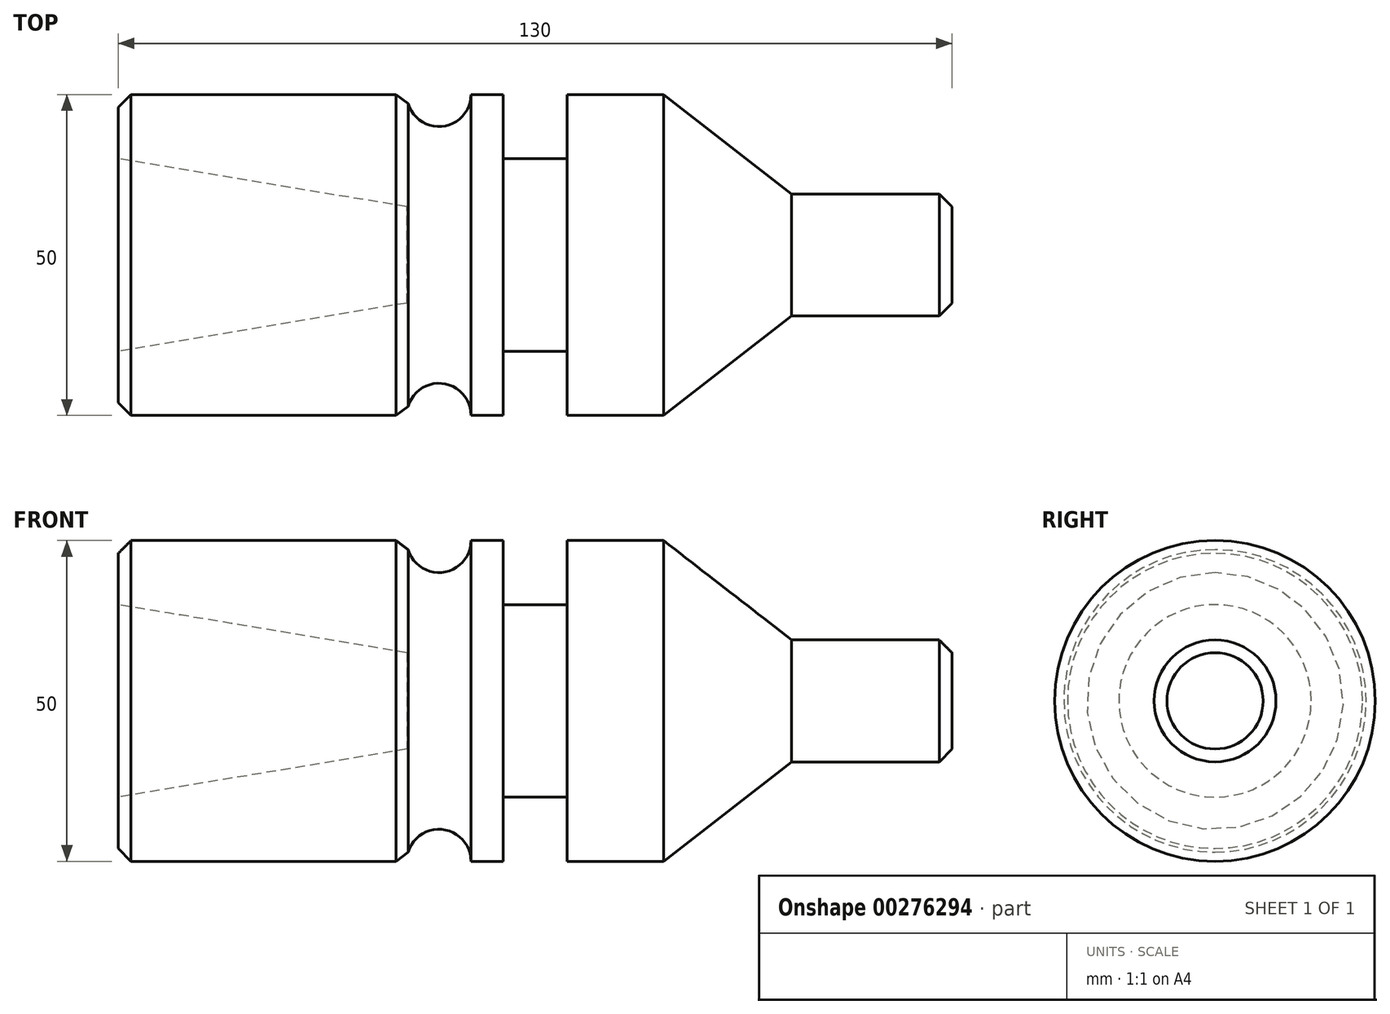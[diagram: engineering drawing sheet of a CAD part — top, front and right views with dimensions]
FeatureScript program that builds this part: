
annotation { "Feature Type Name" : "Feature", "Feature Type Description" : "" }
export const myFeature = defineFeature(function(context is Context, id is Id, definition is map)
    precondition{}
    {
        {
            var Q0;
            Q0=qCreatedBy(makeId("Front.planeOp"),FACE);
            var sketch = newSketch(context, id + "F0", { "sketchPlane" : qUnion([Q0])});
            skLineSegment(sketch, "E0.top", {"start": v(-62.42, 25) * mm, "end": v(-17.42, 25) * mm});
            skLineSegment(sketch, "E0.left", {"start": v(-62.42, 15) * mm, "end": v(-62.42, 25) * mm});
            skLineSegment(sketch, "E0.right", {"start": v(67.58, 0) * mm, "end": v(67.58, 9.5) * mm});
            skLineSegment(sketch, "E1", {"start": v(-62.42, 25) * mm, "end": v(-62.42, 15) * mm});
            skLineSegment(sketch, "E2", {"start": v(-17.42, 7.5) * mm, "end": v(-17.42, 0) * mm, "construction": true});
            skLineSegment(sketch, "E3", {"start": v(-17.42, 0) * mm, "end": v(-17.42, 7.5) * mm});
            skLineSegment(sketch, "E4", {"start": v(-62.42, 15) * mm, "end": v(-17.42, 7.5) * mm});
            skArc(sketch, "E5", {"start": v(-17.42, 25) * mm, "mid": v(-12.42, 20) * mm, "end": v(-7.42, 25) * mm});
            skLineSegment(sketch, "E6", {"start": v(-7.42, 25) * mm, "end": v(-2.42, 25) * mm});
            skLineSegment(sketch, "E7", {"start": v(-2.42, 25) * mm, "end": v(-2.42, 15) * mm});
            skLineSegment(sketch, "E8", {"start": v(-2.42, 15) * mm, "end": v(7.58, 15) * mm});
            skLineSegment(sketch, "E9", {"start": v(7.58, 15) * mm, "end": v(7.58, 25) * mm});
            skLineSegment(sketch, "E10", {"start": v(7.58, 25) * mm, "end": v(22.58, 25) * mm});
            skLineSegment(sketch, "E11", {"start": v(67.58, 9.5) * mm, "end": v(42.58, 9.5) * mm});
            skLineSegment(sketch, "E12", {"start": v(22.58, 25) * mm, "end": v(42.58, 9.5) * mm});
            skPoint(sketch, "E0.bottom.start.orphan", {"position": v(-62.42, 0) * mm});
            skLineSegment(sketch, "E13", {"start": v(-62.42, 0) * mm, "end": v(79.58, 0) * mm});
            skSolve(sketch);
        }
        {
            var Q0;
            Q0=makeQuery(id+"F0.imprint","IMPRINT",FACE,{"disambiguationData":[TD([[makeQuery(id+"F0.imprint","IMPRINT",EDGE,{"derivedFrom":sQuery(id+"F0.wireOp",EDGE,"E0.top")}),-1.0]])]});
            var Q1;
            Q1=sQuery(id+"F0.wireOp",EDGE,"E13");
            revolve(context, id + "F1", {"entities" : qUnion([Q0]), "axis" : qUnion([Q1]), "revolveType" : RevolveType.FULL});
        }
        {
            var Q0;
            Q0=makeQuery(id+"F1.opRevolve","SWEPT_EDGE",EDGE,{"disambiguationData":[OSD([sQuery(id+"F0.wireOp",EDGE,"E0.top"),sQuery(id+"F0.wireOp",EDGE,"E1")])]});
            var Q1;
            Q1=makeQuery(id+"F1.opRevolve","SWEPT_EDGE",EDGE,{"disambiguationData":[OSD([sQuery(id+"F0.wireOp",EDGE,"E0.right"),sQuery(id+"F0.wireOp",EDGE,"E11")])]});
            chamfer(context, id + "F2", {"entities" : qUnion([Q0, Q1]), "width" : 2 * mm, "tangentPropagation" : true});
        }
    });
